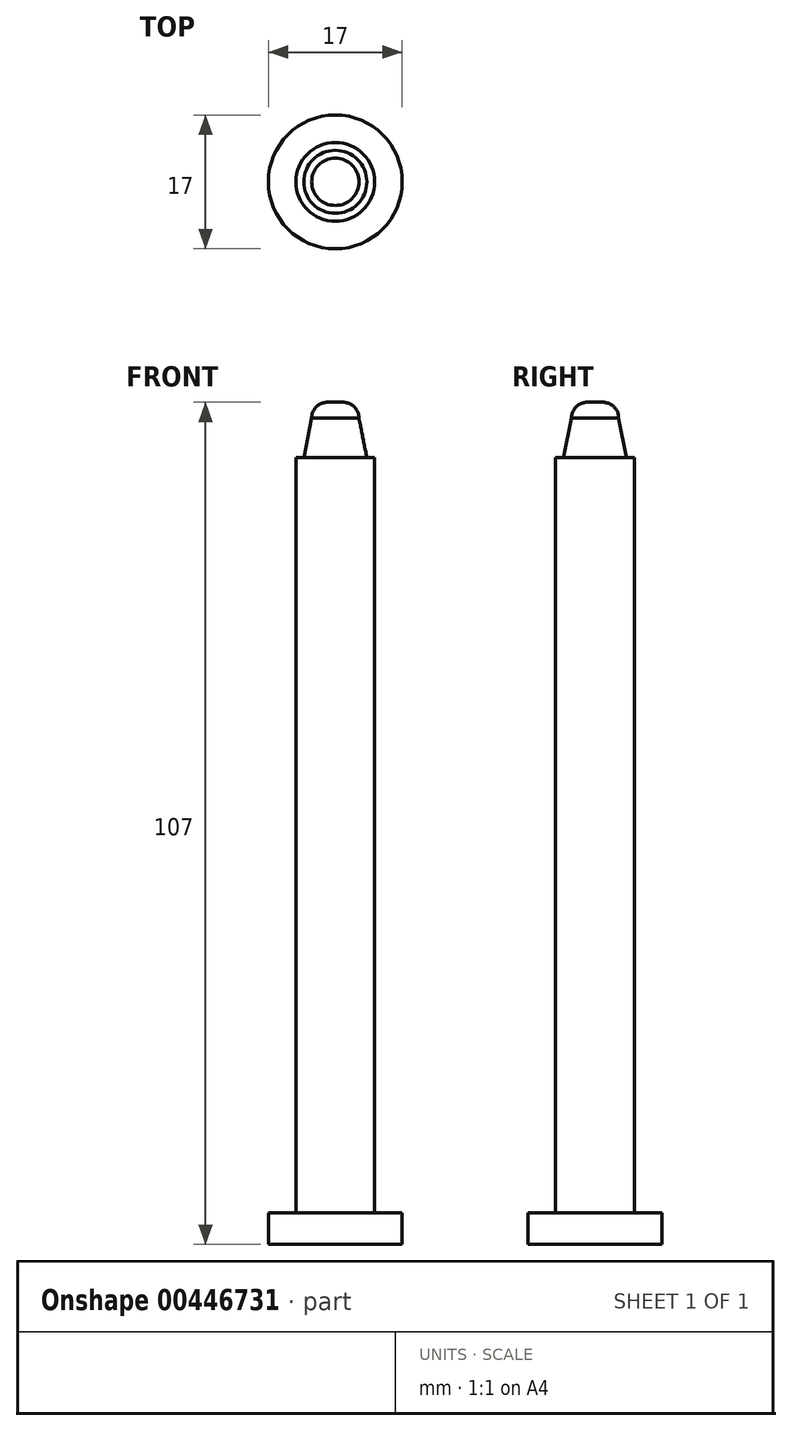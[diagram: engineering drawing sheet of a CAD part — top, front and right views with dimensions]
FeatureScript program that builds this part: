
annotation { "Feature Type Name" : "Feature", "Feature Type Description" : "" }
export const myFeature = defineFeature(function(context is Context, id is Id, definition is map)
    precondition{}
    {
        {
            var Q0;
            Q0=qCreatedBy(makeId("Top.planeOp"),FACE);
            var sketch = newSketch(context, id + "F0", { "sketchPlane" : qUnion([Q0])});
            skCircle(sketch, "E0", {"center": v(0, 0) * mm, "radius": 8.5 * mm});
            skSolve(sketch);
        }
        {
            var Q0;
            Q0=qSketchRegion(id+"F0",true);
            extrude(context, id + "F1", {"entities" : qUnion([Q0]), "depth" : 4 * mm});
        }
        {
            var Q0;
            Q0=qCreatedBy(makeId("Top.planeOp"),FACE);
            var sketch = newSketch(context, id + "F2", { "sketchPlane" : qUnion([Q0])});
            skCircle(sketch, "E1", {"center": v(0, 0) * mm, "radius": 5 * mm});
            skSolve(sketch);
        }
        {
            var Q0;
            Q0=qSketchRegion(id+"F2",true);
            extrude(context, id + "F3", {"entities" : qUnion([Q0]), "operationType" : NewBodyOperationType.ADD, "depth" : 100 * mm});
        }
        {
            var Q0;
            Q0=qCreatedBy(makeId("Right.planeOp"),FACE);
            var sketch = newSketch(context, id + "F4", { "sketchPlane" : qUnion([Q0])});
            skLineSegment(sketch, "E2", {"start": v(0, 105) * mm, "end": v(0, 100) * mm});
            skLineSegment(sketch, "E3", {"start": v(0, 100) * mm, "end": v(4, 100) * mm});
            skLineSegment(sketch, "E4", {"start": v(4, 100) * mm, "end": v(3, 105) * mm});
            skLineSegment(sketch, "E5", {"start": v(3, 105) * mm, "end": v(0, 105) * mm});
            skSolve(sketch);
        }
        {
            var Q0;
            Q0=makeQuery(id+"F4.imprint","IMPRINT",FACE,{"disambiguationData":[TD([[makeQuery(id+"F4.imprint","IMPRINT",EDGE,{"derivedFrom":sQuery(id+"F4.wireOp",EDGE,"E2")}),1.0]])]});
            var Q1;
            Q1=sQuery(id+"F4.wireOp",EDGE,"E2");
            revolve(context, id + "F5", {"operationType" : NewBodyOperationType.ADD, "entities" : qUnion([Q0]), "axis" : qUnion([Q1]), "revolveType" : RevolveType.FULL});
        }
        {
            var Q0;
            Q0=qCreatedBy(makeId("Right.planeOp"),FACE);
            var sketch = newSketch(context, id + "F6", { "sketchPlane" : qUnion([Q0])});
            skLineSegment(sketch, "E6", {"start": v(0, 107) * mm, "end": v(0, 105) * mm});
            skLineSegment(sketch, "E7", {"start": v(0, 105) * mm, "end": v(3, 105) * mm});
            skLineSegment(sketch, "E8", {"start": v(1, 107) * mm, "end": v(0, 107) * mm});
            skArc(sketch, "E9", {"start": v(3, 105) * mm, "mid": v(2.41, 106.41) * mm, "end": v(1, 107) * mm});
            skSolve(sketch);
        }
        {
            var Q0;
            Q0=makeQuery(id+"F6.imprint","IMPRINT",FACE,{"disambiguationData":[TD([[makeQuery(id+"F6.imprint","IMPRINT",EDGE,{"derivedFrom":sQuery(id+"F6.wireOp",EDGE,"E6")}),1.0]])]});
            var Q1;
            Q1=sQuery(id+"F6.wireOp",EDGE,"E6");
            revolve(context, id + "F7", {"operationType" : NewBodyOperationType.ADD, "entities" : qUnion([Q0]), "axis" : qUnion([Q1]), "revolveType" : RevolveType.FULL});
        }
    });
